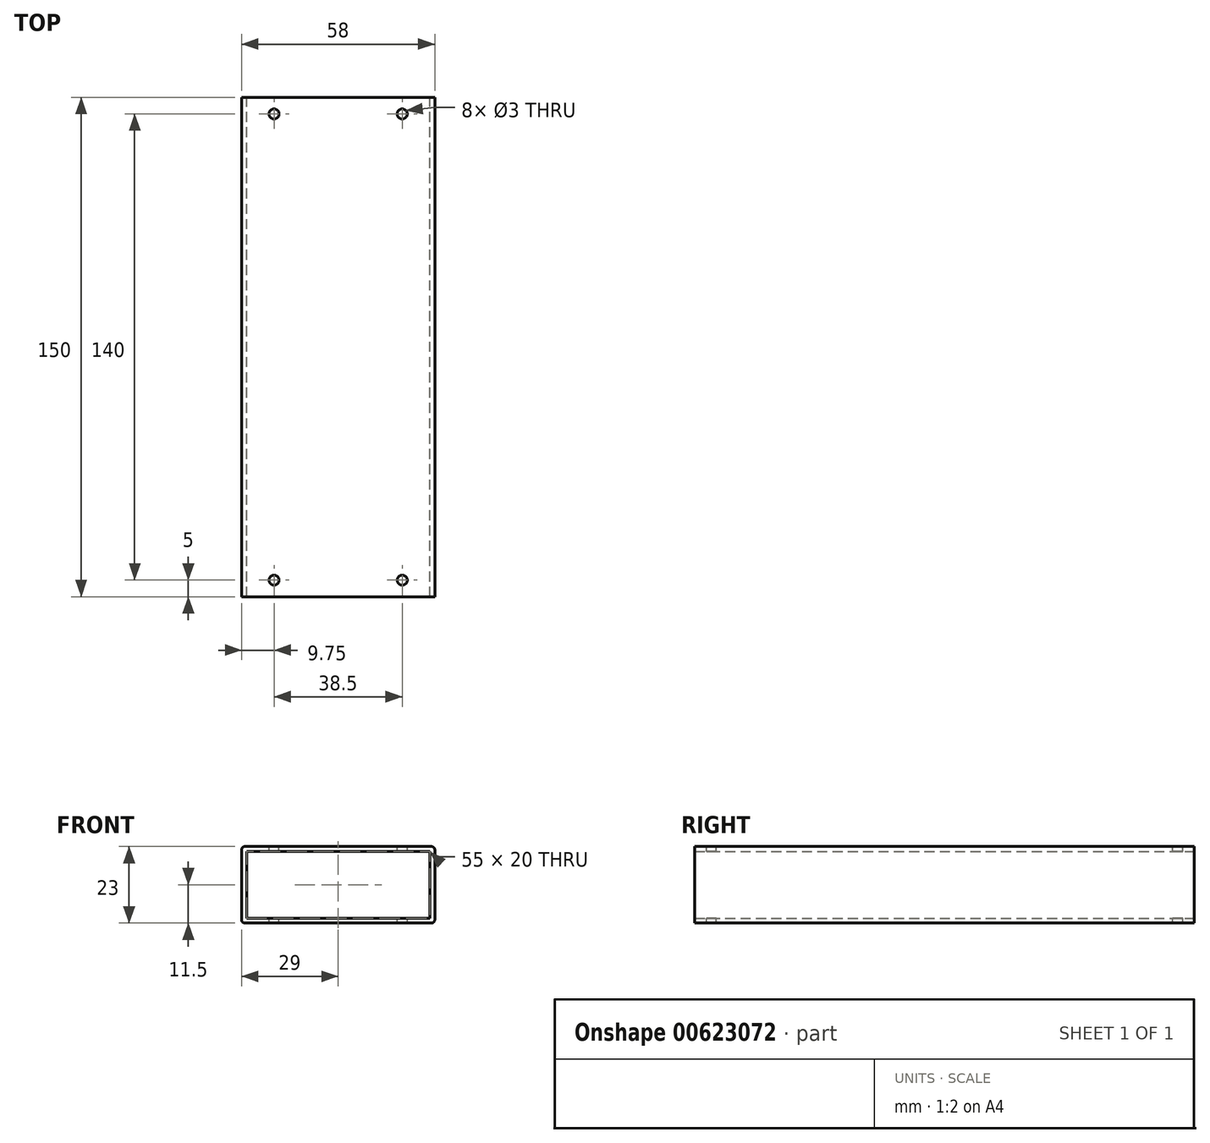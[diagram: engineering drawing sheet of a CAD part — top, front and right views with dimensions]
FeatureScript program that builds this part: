
annotation { "Feature Type Name" : "Feature", "Feature Type Description" : "" }
export const myFeature = defineFeature(function(context is Context, id is Id, definition is map)
    precondition{}
    {
        {
            var Q0;
            Q0=qCreatedBy(makeId("Front.planeOp"),FACE);
            var sketch = newSketch(context, id + "F0", { "sketchPlane" : qUnion([Q0])});
            skLineSegment(sketch, "E0.bottom", {"start": v(-29, 11.5) * mm, "end": v(29, 11.5) * mm});
            skLineSegment(sketch, "E0.top", {"start": v(-29, -11.5) * mm, "end": v(29, -11.5) * mm});
            skLineSegment(sketch, "E0.left", {"start": v(-29, 11.5) * mm, "end": v(-29, -11.5) * mm});
            skLineSegment(sketch, "E0.right", {"start": v(29, 11.5) * mm, "end": v(29, -11.5) * mm});
            skPoint(sketch, "E0.middle", {"position": v(0, 0) * mm});
            skLineSegment(sketch, "E1.bottom", {"start": v(-27.5, 10) * mm, "end": v(27.5, 10) * mm});
            skLineSegment(sketch, "E1.top", {"start": v(-27.5, -10) * mm, "end": v(27.5, -10) * mm});
            skLineSegment(sketch, "E1.left", {"start": v(-27.5, 10) * mm, "end": v(-27.5, -10) * mm});
            skLineSegment(sketch, "E1.right", {"start": v(27.5, 10) * mm, "end": v(27.5, -10) * mm});
            skSolve(sketch);
        }
        {
            var Q0;
            Q0=makeQuery(id+"F0.imprint","IMPRINT",FACE,{"disambiguationData":[TD([[makeQuery(id+"F0.imprint","IMPRINT",EDGE,{"derivedFrom":sQuery(id+"F0.wireOp",EDGE,"E0.bottom")}),-1.0]])]});
            extrude(context, id + "F1", {"entities" : qUnion([Q0]), "depth" : 150 * mm, "offsetDistance" : 25 * mm});
        }
        {
            var Q0;
            Q0=makeQuery(id+"F1.opExtrude","SWEPT_EDGE",EDGE,{"disambiguationData":[OSD([sQuery(id+"F0.wireOp",EDGE,"E0.bottom"),sQuery(id+"F0.wireOp",EDGE,"E0.left")])]});
            var Q1;
            Q1=makeQuery(id+"F1.opExtrude","SWEPT_EDGE",EDGE,{"disambiguationData":[OSD([sQuery(id+"F0.wireOp",EDGE,"E0.bottom"),sQuery(id+"F0.wireOp",EDGE,"E0.right")])]});
            var Q2;
            Q2=makeQuery(id+"F1.opExtrude","SWEPT_EDGE",EDGE,{"disambiguationData":[OSD([sQuery(id+"F0.wireOp",EDGE,"E0.top"),sQuery(id+"F0.wireOp",EDGE,"E0.left")])]});
            var Q3;
            Q3=makeQuery(id+"F1.opExtrude","SWEPT_EDGE",EDGE,{"disambiguationData":[OSD([sQuery(id+"F0.wireOp",EDGE,"E0.top"),sQuery(id+"F0.wireOp",EDGE,"E0.right")])]});
            fillet(context, id + "F2", {"entities" : qUnion([Q0, Q1, Q2, Q3]), "radius" : 1 * mm, "tangentPropagation" : true, "allowEdgeOverflow" : false});
        }
        {
            var Q0;
            Q0=qCreatedBy(makeId("Top.planeOp"),FACE);
            var sketch = newSketch(context, id + "F3", { "sketchPlane" : qUnion([Q0])});
            skCircle(sketch, "E2", {"center": v(-19.25, -5) * mm, "radius": 1.5 * mm});
            skCircle(sketch, "E3", {"center": v(19.25, -5) * mm, "radius": 1.5 * mm});
            skCircle(sketch, "E4", {"center": v(-19.25, -145) * mm, "radius": 1.5 * mm});
            skCircle(sketch, "E5", {"center": v(19.25, -145) * mm, "radius": 1.5 * mm});
            skSolve(sketch);
        }
        {
            var Q0;
            Q0=makeQuery(id+"F3.imprint","IMPRINT",FACE,{"disambiguationData":[TD([[makeQuery(id+"F3.imprint","IMPRINT",EDGE,{"derivedFrom":sQuery(id+"F3.wireOp",EDGE,"E2")}),1.0]])]});
            extrude(context, id + "F4", {"entities" : qUnion([Q0]), "operationType" : NewBodyOperationType.REMOVE, "endBound" : BoundingType.SYMMETRIC, "oppositeDirection" : true, "depth" : 30 * mm, "offsetDistance" : 25 * mm});
        }
        {
            var Q0;
            Q0=makeQuery(id+"F3.imprint","IMPRINT",FACE,{"disambiguationData":[TD([[makeQuery(id+"F3.imprint","IMPRINT",EDGE,{"derivedFrom":sQuery(id+"F3.wireOp",EDGE,"E3")}),1.0]])]});
            extrude(context, id + "F5", {"entities" : qUnion([Q0]), "operationType" : NewBodyOperationType.REMOVE, "endBound" : BoundingType.SYMMETRIC, "oppositeDirection" : true, "depth" : 30 * mm, "offsetDistance" : 25 * mm});
        }
        {
            var Q0;
            Q0=makeQuery(id+"F3.imprint","IMPRINT",FACE,{"disambiguationData":[TD([[makeQuery(id+"F3.imprint","IMPRINT",EDGE,{"derivedFrom":sQuery(id+"F3.wireOp",EDGE,"E5")}),1.0]])]});
            var Q1;
            Q1=makeQuery(id+"F3.imprint","IMPRINT",FACE,{"disambiguationData":[TD([[makeQuery(id+"F3.imprint","IMPRINT",EDGE,{"derivedFrom":sQuery(id+"F3.wireOp",EDGE,"E4")}),1.0]])]});
            extrude(context, id + "F6", {"entities" : qUnion([Q0, Q1]), "operationType" : NewBodyOperationType.REMOVE, "endBound" : BoundingType.SYMMETRIC, "oppositeDirection" : true, "depth" : 30 * mm, "offsetDistance" : 25 * mm});
        }
    });
